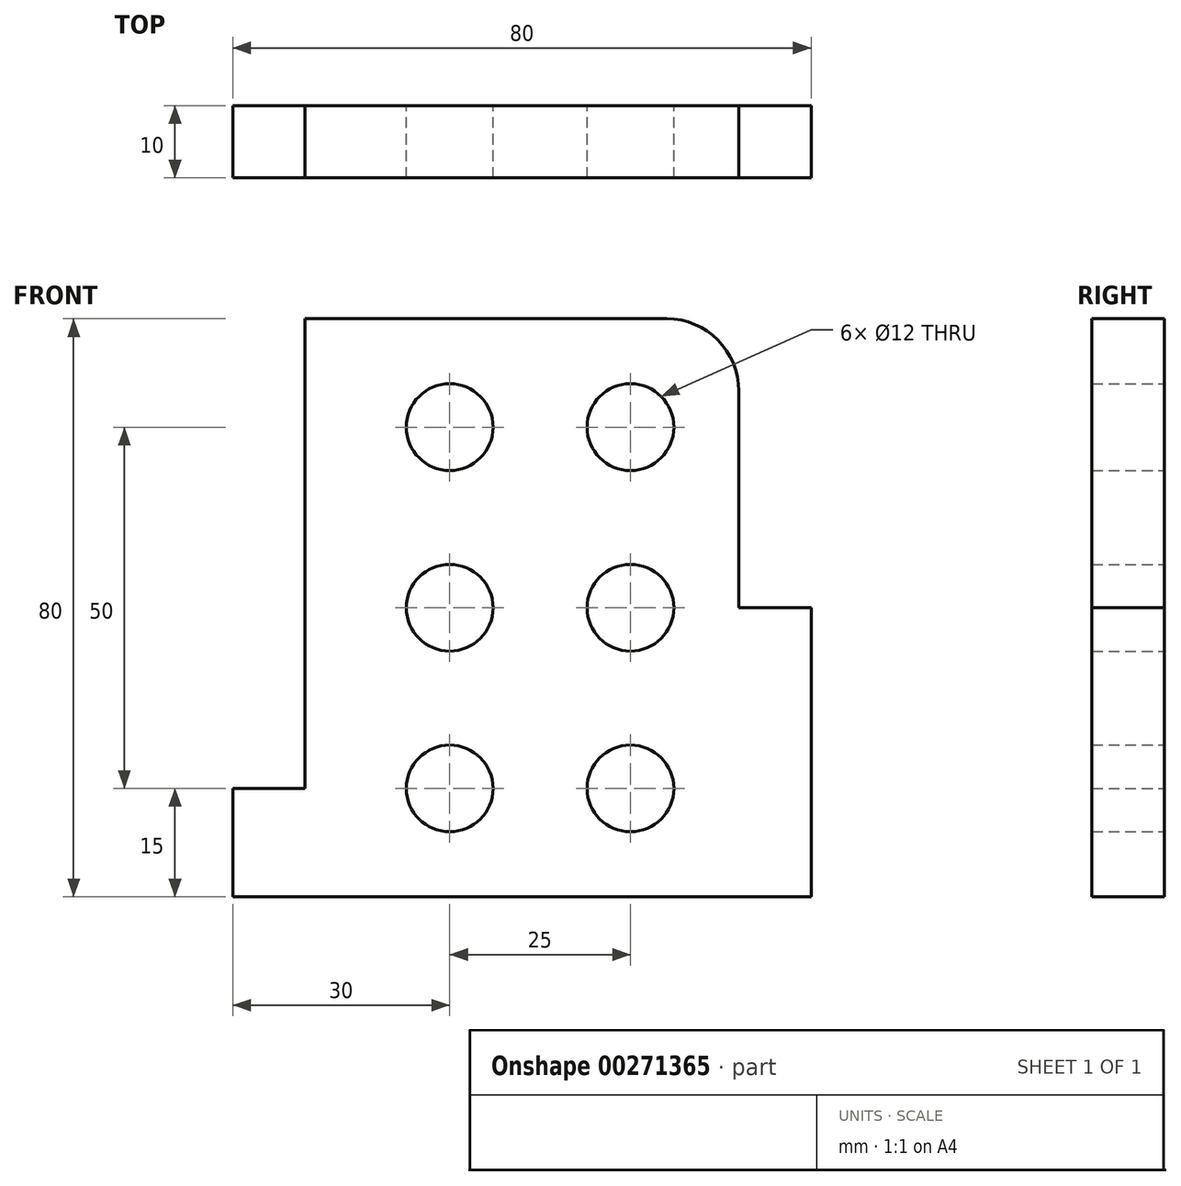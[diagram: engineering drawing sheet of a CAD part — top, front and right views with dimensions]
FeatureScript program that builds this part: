
annotation { "Feature Type Name" : "Feature", "Feature Type Description" : "" }
export const myFeature = defineFeature(function(context is Context, id is Id, definition is map)
    precondition{}
    {
        {
            var Q0;
            Q0=qCreatedBy(makeId("Front.planeOp"),FACE);
            var sketch = newSketch(context, id + "F0", { "sketchPlane" : qUnion([Q0])});
            skLineSegment(sketch, "E0.bottom", {"start": v(0, 0) * mm, "end": v(80, 0) * mm});
            skLineSegment(sketch, "E0.left", {"start": v(0, 0) * mm, "end": v(0, 15) * mm});
            skLineSegment(sketch, "E1", {"start": v(10, 15) * mm, "end": v(10, 80) * mm});
            skLineSegment(sketch, "E2", {"start": v(0, 15) * mm, "end": v(10, 15) * mm});
            skLineSegment(sketch, "E3", {"start": v(80, 40) * mm, "end": v(80, 0) * mm});
            skPoint(sketch, "E4.visualSharp", {"position": v(70, 80) * mm});
            skArc(sketch, "E4.filletArc", {"start": v(70, 70) * mm, "mid": v(67.07, 77.07) * mm, "end": v(60, 80) * mm});
            skLineSegment(sketch, "E5", {"start": v(60, 80) * mm, "end": v(10, 80) * mm});
            skLineSegment(sketch, "E6", {"start": v(70, 70) * mm, "end": v(70, 40) * mm});
            skLineSegment(sketch, "E7", {"start": v(70, 40) * mm, "end": v(80, 40) * mm});
            skCircle(sketch, "E8", {"center": v(30, 65) * mm, "radius": 6 * mm});
            skCircle(sketch, "E9", {"center": v(30, 40) * mm, "radius": 6 * mm});
            skCircle(sketch, "E10", {"center": v(30, 15) * mm, "radius": 6 * mm});
            skCircle(sketch, "E11", {"center": v(55, 65) * mm, "radius": 6 * mm});
            skCircle(sketch, "E12", {"center": v(55, 40) * mm, "radius": 6 * mm});
            skCircle(sketch, "E13", {"center": v(55, 15) * mm, "radius": 6 * mm});
            skSolve(sketch);
        }
        {
            var Q0;
            Q0 = qSketchRegion(id + "F0", true);
            extrude(context, id + "F1", {"entities" : qUnion([Q0]), "depth" : 10 * mm});
        }
    });
